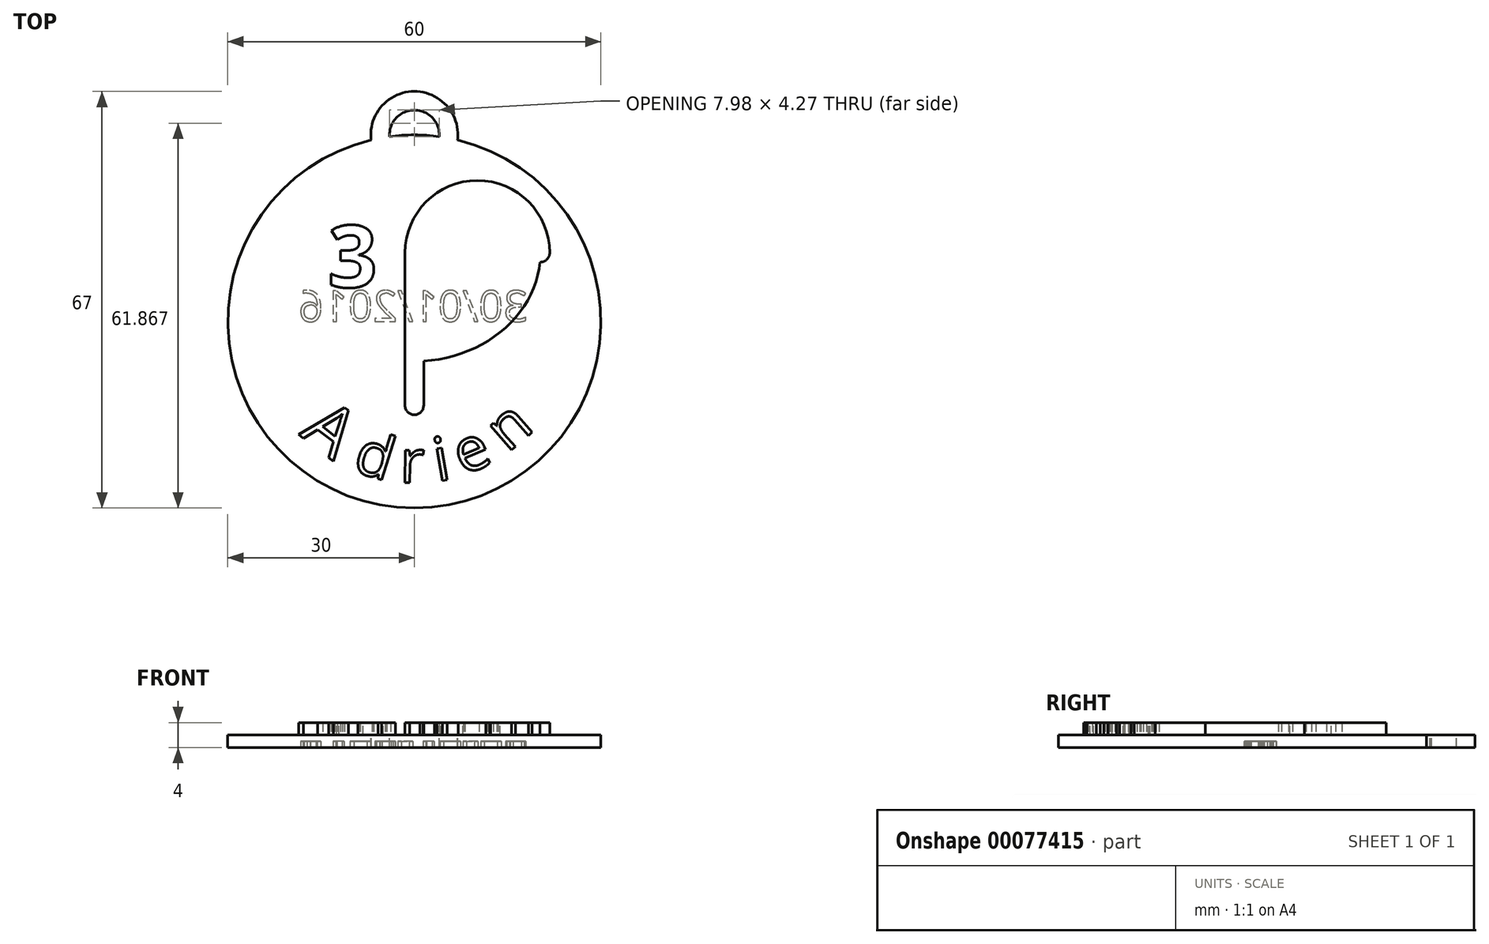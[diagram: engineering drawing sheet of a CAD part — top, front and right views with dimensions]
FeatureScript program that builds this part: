
annotation { "Feature Type Name" : "Feature", "Feature Type Description" : "" }
export const myFeature = defineFeature(function(context is Context, id is Id, definition is map)
    precondition{}
    {
        {
            var Q0;
            Q0=qCreatedBy(makeId("Top.planeOp"),FACE);
            var sketch = newSketch(context, id + "F0", { "sketchPlane" : qUnion([Q0])});
            skCircle(sketch, "E0", {"center": v(0, 0) * mm, "radius": 30 * mm});
            skSolve(sketch);
        }
        {
            var Q0;
            Q0=qSketchRegion(id+"F0",true);
            extrude(context, id + "F1", {"entities" : qUnion([Q0]), "oppositeDirection" : true, "depth" : 2 * mm});
        }
        {
            var Q0;
            Q0=qCreatedBy(makeId("Top.planeOp"),FACE);
            var sketch = newSketch(context, id + "F2", { "sketchPlane" : qUnion([Q0])});
            skEllipticalArc(sketch, "E1", {});
            skLineSegment(sketch, "E2", {"start": v(0, 0) * mm, "end": v(0, 30) * mm, "construction": true});
            skLineSegment(sketch, "E3", {"start": v(0, 11.04) * mm, "end": v(0, -13.5) * mm});
            skArc(sketch, "E4", {"start": v(20.27, 11.04) * mm, "mid": v(10.13, 21.17) * mm, "end": v(0, 11.04) * mm});
            skLineSegment(sketch, "E5", {"start": v(0, 11.04) * mm, "end": v(-16.84, 20.76) * mm, "construction": true});
            skLineSegment(sketch, "E6", {"start": v(0, 11.04) * mm, "end": v(-20.27, 11.04) * mm, "construction": true});
            skArc(sketch, "E7.0.startCap", {"start": v(-1.5, 11.04) * mm, "mid": v(0, 12.54) * mm, "end": v(1.5, 11.04) * mm});
            skArc(sketch, "E7.0.endCap", {"start": v(1.5, -13.5) * mm, "mid": v(0, -15) * mm, "end": v(-1.5, -13.5) * mm});
            skLineSegment(sketch, "E7.0.left", {"start": v(1.5, 11.04) * mm, "end": v(1.5, -13.5) * mm});
            skLineSegment(sketch, "E7.0.right", {"start": v(-1.5, 11.04) * mm, "end": v(-1.5, -13.5) * mm});
            skArc(sketch, "E8.0.startCap", {"start": v(21.77, 11.04) * mm, "mid": v(20.27, 9.54) * mm, "end": v(18.77, 11.04) * mm});
            skArc(sketch, "E8.0.endCap", {"start": v(1.5, 11.04) * mm, "mid": v(0, 9.54) * mm, "end": v(-1.5, 11.04) * mm});
            skArc(sketch, "E8.0.left", {"start": v(18.77, 11.04) * mm, "mid": v(10.13, 19.67) * mm, "end": v(1.5, 11.04) * mm});
            skArc(sketch, "E8.0.right", {"start": v(21.77, 11.04) * mm, "mid": v(10.13, 22.67) * mm, "end": v(-1.5, 11.04) * mm});
            skArc(sketch, "E8.1.startCap", {"start": v(-18.02, 21.68) * mm, "mid": v(-15.91, 21.95) * mm, "end": v(-15.65, 19.84) * mm});
            skArc(sketch, "E8.1.endCap", {"start": v(18.77, 11.04) * mm, "mid": v(20.27, 12.54) * mm, "end": v(21.77, 11.04) * mm});
            skFitSpline(sketch, "E8.1.left", {"points": [v(18.7, 9.5) * mm, v(18.8, 11.04) * mm, v(18.7, 12.6) * mm, v(18.36, 14.63) * mm, v(17.66, 16.6) * mm, v(16.63, 18.49) * mm, v(15.37, 20.3) * mm, v(13.44, 22.32) * mm, v(11.07, 24) * mm, v(8.94, 25.1) * mm, v(6.7, 26.01) * mm, v(4.32, 26.63) * mm, v(1.87, 26.95) * mm, v(0, 27.03) * mm, v(-1.87, 26.95) * mm, v(-4.32, 26.63) * mm, v(-6.7, 26.01) * mm, v(-8.94, 25.1) * mm, v(-11.07, 24) * mm, v(-13.44, 22.32) * mm, v(-15.37, 20.3) * mm, v(-16.63, 18.49) * mm, v(-17.66, 16.6) * mm, v(-18.36, 14.63) * mm, v(-18.7, 12.6) * mm, v(-18.8, 11.04) * mm, v(-18.7, 9.5) * mm, v(-18.36, 7.46) * mm, v(-17.66, 5.48) * mm, v(-16.63, 3.6) * mm, v(-15.37, 1.8) * mm, v(-13.44, -0.24) * mm, v(-11.07, -1.92) * mm, v(-8.94, -3.02) * mm, v(-6.7, -3.93) * mm, v(-4.32, -4.55) * mm, v(-1.87, -4.86) * mm, v(0, -4.94) * mm, v(1.87, -4.86) * mm, v(4.32, -4.55) * mm, v(6.7, -3.93) * mm, v(8.94, -3.02) * mm, v(11.07, -1.92) * mm, v(13.44, -0.24) * mm, v(15.37, 1.8) * mm, v(16.63, 3.6) * mm, v(17.66, 5.48) * mm, v(18.36, 7.46) * mm, v(18.7, 9.5) * mm, v(18.8, 11.04) * mm, v(18.7, 12.6) * mm]});
            skFitSpline(sketch, "E8.1.right", {"points": [v(21.7, 9.15) * mm, v(21.8, 11.04) * mm, v(21.7, 12.93) * mm, v(21.27, 15.42) * mm, v(20.42, 17.81) * mm, v(19.18, 20.07) * mm, v(17.69, 22.22) * mm, v(15.4, 24.61) * mm, v(12.65, 26.56) * mm, v(10.2, 27.83) * mm, v(7.62, 28.88) * mm, v(4.92, 29.58) * mm, v(2.12, 29.94) * mm, v(0, 30.03) * mm, v(-2.12, 29.94) * mm, v(-4.92, 29.58) * mm, v(-7.62, 28.88) * mm, v(-10.2, 27.83) * mm, v(-12.65, 26.56) * mm, v(-15.4, 24.61) * mm, v(-17.69, 22.22) * mm, v(-19.18, 20.07) * mm, v(-20.42, 17.81) * mm, v(-21.27, 15.42) * mm, v(-21.7, 12.93) * mm, v(-21.8, 11.04) * mm, v(-21.7, 9.15) * mm, v(-21.27, 6.67) * mm, v(-20.42, 4.27) * mm, v(-19.18, 2) * mm, v(-17.69, -0.14) * mm, v(-15.4, -2.53) * mm, v(-12.65, -4.48) * mm, v(-10.2, -5.75) * mm, v(-7.62, -6.8) * mm, v(-4.92, -7.5) * mm, v(-2.12, -7.86) * mm, v(0, -7.95) * mm, v(2.12, -7.86) * mm, v(4.92, -7.5) * mm, v(7.62, -6.8) * mm, v(10.2, -5.75) * mm, v(12.65, -4.48) * mm, v(15.4, -2.53) * mm, v(17.69, -0.14) * mm, v(19.18, 2) * mm, v(20.42, 4.27) * mm, v(21.27, 6.67) * mm, v(21.7, 9.15) * mm, v(21.8, 11.04) * mm, v(21.7, 12.93) * mm]});
            const initialGuessF2  = {"E1": [0, 0.011041626236194823, 1, 0, 0.020266667008310185, 0.017458373763805178, 2.5511335140588507, 0]};
            skSetInitialGuess(sketch, initialGuessF2);
            skSolve(sketch);
        }
        {
            var Q0;
            {var subQ0=sQuery(id+"F2.wireOp",EDGE,"E8.1.startCap");Q0=makeQuery(id+"F2.imprint","IMPRINT",FACE,{"disambiguationData":[TD([[makeQuery(id+"F2.imprint","IMPRINT",EDGE,{"derivedFrom":subQ0}),-1.0]])]});}
            var Q1;
            {var subQ0=sQuery(id+"F2.wireOp",EDGE,"E7.0.right");var subQ1=sQuery(id+"F2.wireOp",EDGE,"E1");var subQ2=makeQuery(id+"F2.imprint","INTERSECT",VERTEX,{"derivedFrom":[subQ1,subQ0]});Q1=makeQuery(id+"F2.imprint","IMPRINT",FACE,{"disambiguationData":[TD([[makeQuery(id+"F2.imprint","IMPRINT",EDGE,{"disambiguationData":[TD([[subQ2,-1.0]])],"derivedFrom":subQ1}),1.0]])]});}
            var Q2;
            {var subQ0=sQuery(id+"F2.wireOp",EDGE,"E3");var subQ1=sQuery(id+"F2.wireOp",EDGE,"E1");var subQ2=makeQuery(id+"F2.imprint","INTERSECT",VERTEX,{"derivedFrom":[subQ1,subQ0]});Q2=makeQuery(id+"F2.imprint","IMPRINT",FACE,{"disambiguationData":[TD([[makeQuery(id+"F2.imprint","IMPRINT",EDGE,{"disambiguationData":[TD([[subQ2,-1.0]])],"derivedFrom":subQ1}),1.0]])]});}
            var Q3;
            {var subQ0=sQuery(id+"F2.wireOp",EDGE,"E7.0.right");var subQ1=sQuery(id+"F2.wireOp",EDGE,"E1");var subQ2=makeQuery(id+"F2.imprint","INTERSECT",VERTEX,{"derivedFrom":[subQ1,subQ0]});Q3=makeQuery(id+"F2.imprint","IMPRINT",FACE,{"disambiguationData":[TD([[makeQuery(id+"F2.imprint","IMPRINT",EDGE,{"disambiguationData":[TD([[subQ2,-1.0]])],"derivedFrom":subQ1}),-1.0]])]});}
            var Q4;
            {var subQ0=sQuery(id+"F2.wireOp",EDGE,"E3");var subQ1=sQuery(id+"F2.wireOp",EDGE,"E1");var subQ2=makeQuery(id+"F2.imprint","INTERSECT",VERTEX,{"derivedFrom":[subQ1,subQ0]});Q4=makeQuery(id+"F2.imprint","IMPRINT",FACE,{"disambiguationData":[TD([[makeQuery(id+"F2.imprint","IMPRINT",EDGE,{"disambiguationData":[TD([[subQ2,-1.0]])],"derivedFrom":subQ1}),-1.0]])]});}
            var Q5;
            {var subQ0=sQuery(id+"F2.wireOp",EDGE,"E7.0.left");var subQ1=sQuery(id+"F2.wireOp",EDGE,"E1");var subQ2=makeQuery(id+"F2.imprint","INTERSECT",VERTEX,{"derivedFrom":[subQ1,subQ0]});Q5=makeQuery(id+"F2.imprint","IMPRINT",FACE,{"disambiguationData":[TD([[makeQuery(id+"F2.imprint","IMPRINT",EDGE,{"disambiguationData":[TD([[subQ2,-1.0]])],"derivedFrom":subQ1}),-1.0]])]});}
            var Q6;
            {var subQ0=sQuery(id+"F2.wireOp",EDGE,"E7.0.left");var subQ1=sQuery(id+"F2.wireOp",EDGE,"E1");var subQ2=makeQuery(id+"F2.imprint","INTERSECT",VERTEX,{"derivedFrom":[subQ1,subQ0]});Q6=makeQuery(id+"F2.imprint","IMPRINT",FACE,{"disambiguationData":[TD([[makeQuery(id+"F2.imprint","IMPRINT",EDGE,{"disambiguationData":[TD([[subQ2,-1.0]])],"derivedFrom":subQ1}),1.0]])]});}
            var Q7;
            {var subQ0=sQuery(id+"F2.wireOp",EDGE,"E4");var subQ1=sQuery(id+"F2.wireOp",EDGE,"E1");var subQ2=makeQuery(id+"F2.imprint","INTERSECT",VERTEX,{"derivedFrom":[subQ1,subQ0]});Q7=makeQuery(id+"F2.imprint","IMPRINT",FACE,{"disambiguationData":[TD([[makeQuery(id+"F2.imprint","IMPRINT",EDGE,{"disambiguationData":[TD([[subQ2,1.0]])],"derivedFrom":subQ1}),-1.0]])]});}
            var Q8;
            {var subQ0=sQuery(id+"F2.wireOp",EDGE,"E4");var subQ1=sQuery(id+"F2.wireOp",EDGE,"E1");var subQ2=makeQuery(id+"F2.imprint","INTERSECT",VERTEX,{"derivedFrom":[subQ1,subQ0]});Q8=makeQuery(id+"F2.imprint","IMPRINT",FACE,{"disambiguationData":[TD([[makeQuery(id+"F2.imprint","IMPRINT",EDGE,{"disambiguationData":[TD([[subQ2,1.0]])],"derivedFrom":subQ1}),1.0]])]});}
            var Q9;
            {var subQ5=sQuery(id+"F2.wireOp",EDGE,"E8.0.left");Q9=makeQuery(id+"F2.imprint","IMPRINT",FACE,{"disambiguationData":[TD([[makeQuery(id+"F2.imprint","IMPRINT",EDGE,{"derivedFrom":subQ5}),-1.0]])]});}
            var Q10;
            {var subQ5=sQuery(id+"F2.wireOp",EDGE,"E8.0.right");Q10=makeQuery(id+"F2.imprint","IMPRINT",FACE,{"disambiguationData":[TD([[makeQuery(id+"F2.imprint","IMPRINT",EDGE,{"derivedFrom":subQ5}),1.0]])]});}
            var Q11;
            {var subQ0=sQuery(id+"F2.wireOp",EDGE,"E4");var subQ1=sQuery(id+"F2.wireOp",EDGE,"E3");var subQ2=makeQuery(id+"F2.imprint","INTERSECT",VERTEX,{"derivedFrom":[subQ1,subQ0]});Q11=makeQuery(id+"F2.imprint","IMPRINT",FACE,{"disambiguationData":[TD([[makeQuery(id+"F2.imprint","IMPRINT",EDGE,{"disambiguationData":[TD([[subQ2,-1.0]])],"derivedFrom":subQ1}),-1.0]])]});}
            var Q12;
            {var subQ0=sQuery(id+"F2.wireOp",EDGE,"E4");var subQ1=sQuery(id+"F2.wireOp",EDGE,"E3");var subQ2=makeQuery(id+"F2.imprint","INTERSECT",VERTEX,{"derivedFrom":[subQ1,subQ0]});Q12=makeQuery(id+"F2.imprint","IMPRINT",FACE,{"disambiguationData":[TD([[makeQuery(id+"F2.imprint","IMPRINT",EDGE,{"disambiguationData":[TD([[subQ2,-1.0]])],"derivedFrom":subQ1}),1.0]])]});}
            var Q13;
            {var subQ0=sQuery(id+"F2.wireOp",EDGE,"E8.0.endCap");var subQ1=sQuery(id+"F2.wireOp",EDGE,"E3");var subQ2=makeQuery(id+"F2.imprint","INTERSECT",VERTEX,{"derivedFrom":[subQ1,subQ0]});Q13=makeQuery(id+"F2.imprint","IMPRINT",FACE,{"disambiguationData":[TD([[makeQuery(id+"F2.imprint","IMPRINT",EDGE,{"disambiguationData":[TD([[subQ2,-1.0]])],"derivedFrom":subQ1}),-1.0]])]});}
            var Q14;
            {var subQ0=sQuery(id+"F2.wireOp",EDGE,"E8.0.endCap");var subQ1=sQuery(id+"F2.wireOp",EDGE,"E3");var subQ2=makeQuery(id+"F2.imprint","INTERSECT",VERTEX,{"derivedFrom":[subQ1,subQ0]});Q14=makeQuery(id+"F2.imprint","IMPRINT",FACE,{"disambiguationData":[TD([[makeQuery(id+"F2.imprint","IMPRINT",EDGE,{"disambiguationData":[TD([[subQ2,-1.0]])],"derivedFrom":subQ1}),1.0]])]});}
            var Q15;
            {var subQ1=sQuery(id+"F2.wireOp",EDGE,"E7.0.endCap");Q15=makeQuery(id+"F2.imprint","IMPRINT",FACE,{"disambiguationData":[TD([[makeQuery(id+"F2.imprint","IMPRINT",EDGE,{"derivedFrom":subQ1}),-1.0]])]});}
            extrude(context, id + "F3", {"entities" : qUnion([Q0, Q1, Q2, Q3, Q4, Q5, Q6, Q7, Q8, Q9, Q10, Q11, Q12, Q13, Q14, Q15]), "operationType" : NewBodyOperationType.ADD, "depth" : 2 * mm});
        }
        {
            var Q0;
            Q0=qCreatedBy(makeId("Top.planeOp"),FACE);
            var sketch = newSketch(context, id + "F4", { "sketchPlane" : qUnion([Q0])});
            skText(sketch, "E9", { "text": "3", "fontName": "OpenSans-Bold.ttf"});
            skText(sketch, "E10", { "text": "D", "fontName": "OpenSans-Bold.ttf"});
            const initialGuessF4  = {"E9": [-0.0139, 0.0055, 1, 0, 0.01], "E10": [0.0055, 0.0055, 1, 0, 0.01]};
            skSetInitialGuess(sketch, initialGuessF4);
            skSolve(sketch);
        }
        {
            var Q0;
            Q0=qSketchRegion(id+"F4",true);
            extrude(context, id + "F5", {"entities" : qUnion([Q0]), "operationType" : NewBodyOperationType.ADD, "depth" : 2 * mm});
        }
        {
            var Q0;
            {var subQ8=sQuery(id+"F0.wireOp",EDGE,"E0");Q0=makeQuery(id+"F3.boolean.opBoolean","SPLIT",FACE,{"disambiguationData":[TD([makeQuery(id+"F1.opExtrude","SWEPT_FACE",FACE,{"disambiguationData":[OSD([subQ8])]})])],"derivedFrom":makeQuery(id+"F1.opExtrude","CAP_FACE",FACE,{"disambiguationData":[OSD([subQ8])],"isStart":true})});}
            var sketch = newSketch(context, id + "F6", { "sketchPlane" : qUnion([Q0])});
            skCircle(sketch, "E11.0", {"center": v(0, 0) * mm, "radius": 26 * mm, "construction": true});
            skText(sketch, "E12", { "text": "A", "fontName": "OpenSans-Regular.ttf"});
            skText(sketch, "E13", { "text": "d", "fontName": "OpenSans-Regular.ttf"});
            skText(sketch, "E14", { "text": "r", "fontName": "OpenSans-Regular.ttf"});
            skText(sketch, "E15", { "text": "i", "fontName": "OpenSans-Regular.ttf"});
            skText(sketch, "E16", { "text": "e", "fontName": "OpenSans-Regular.ttf"});
            skText(sketch, "E17", { "text": "n", "fontName": "OpenSans-Regular.ttf"});
            const initialGuessF6  = {"E12": [-0.01858, -0.0182, 0.78988, -0.61326, 0.008], "E13": [-0.01014, -0.02394, 0.95474, -0.29746, 0.007], "E14": [-0.00237, -0.0259, 0.99984, -0.01762, 0.007], "E15": [0.00368, -0.02574, 0.9848, 0.17368, 0.007], "E16": [0.00785, -0.02479, 0.92036, 0.39107, 0.007], "E17": [0.01502, -0.02122, 0.75459, 0.6562, 0.007]};
            skSetInitialGuess(sketch, initialGuessF6);
            skSolve(sketch);
        }
        {
            var Q0;
            Q0=qSketchRegion(id+"F6",true);
            extrude(context, id + "F7", {"entities" : qUnion([Q0]), "operationType" : NewBodyOperationType.ADD, "depth" : 2 * mm});
        }
        {
            var Q0;
            Q0=qCreatedBy(makeId("Top.planeOp"),FACE);
            var sketch = newSketch(context, id + "F8", { "sketchPlane" : qUnion([Q0])});
            skArc(sketch, "E18", {"start": v(5.48, 29.5) * mm, "mid": v(0, 35.5) * mm, "end": v(-5.48, 29.5) * mm});
            skArc(sketch, "E19.0.startCap", {"start": v(6.97, 29.36) * mm, "mid": v(5.34, 28) * mm, "end": v(3.98, 29.63) * mm});
            skArc(sketch, "E19.0.endCap", {"start": v(-3.98, 29.63) * mm, "mid": v(-5.34, 28) * mm, "end": v(-6.97, 29.36) * mm});
            skArc(sketch, "E19.0.left", {"start": v(3.98, 29.63) * mm, "mid": v(0, 34) * mm, "end": v(-3.98, 29.63) * mm});
            skArc(sketch, "E19.0.right", {"start": v(6.97, 29.36) * mm, "mid": v(0, 37) * mm, "end": v(-6.97, 29.36) * mm});
            skSolve(sketch);
        }
        {
            var Q0;
            Q0=qSketchRegion(id+"F8",true);
            extrude(context, id + "F9", {"entities" : qUnion([Q0]), "operationType" : NewBodyOperationType.ADD, "oppositeDirection" : true, "depth" : 2 * mm});
        }
        {
            var Q0;
            Q0=makeQuery(id+"F9.boolean.opBoolean","MERGE",FACE,{"derivedFrom":[makeQuery(id+"F1.opExtrude","CAP_FACE",FACE,{"disambiguationData":[OSD([sQuery(id+"F0.wireOp",EDGE,"E0")])],"isStart":false}),makeQuery(id+"F9.opExtrude","CAP_FACE",FACE,{"disambiguationData":[OSD([sQuery(id+"F8.wireOp",EDGE,"E19.0.startCap"),sQuery(id+"F8.wireOp",EDGE,"E19.0.endCap"),sQuery(id+"F8.wireOp",EDGE,"E19.0.left"),sQuery(id+"F8.wireOp",EDGE,"E19.0.right")])],"isStart":false})]});
            var sketch = newSketch(context, id + "F10", { "sketchPlane" : qUnion([Q0])});
            skText(sketch, "E20", { "text": "30/01/2016", "fontName": "OpenSans-Regular.ttf"});
            const initialGuessF10  = {"E20": [0.01826, 0, -1, 0, 0.005]};
            skSetInitialGuess(sketch, initialGuessF10);
            skSolve(sketch);
        }
        {
            var Q0;
            Q0=qSketchRegion(id+"F10",true);
            extrude(context, id + "F11", {"entities" : qUnion([Q0]), "operationType" : NewBodyOperationType.REMOVE, "oppositeDirection" : true, "depth" : 1 * mm});
        }
    });
